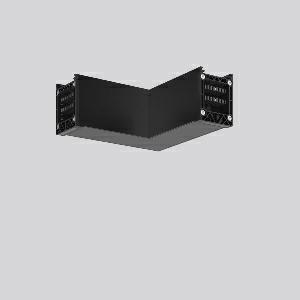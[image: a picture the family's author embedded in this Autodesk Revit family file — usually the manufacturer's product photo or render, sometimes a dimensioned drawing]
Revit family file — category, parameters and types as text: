
# Revit family: linedo_l-verbindung_982773_003_4_29e0
name_source: partatom
category: Lighting Fixtures
units: mm (PartAtom-declared; Revit-internal decimal feet)

## family parameters
Cut with Voids When Loaded = No
Host = Face
Light Source = No
Part Type = Normal
Room Calculation Point = No
Round Connector Dimension = Use Diameter
Shared = No

## types (1)
- LINEDO L-Verbindung
    Apparent Load = 0 VA
    Default Elevation = 1800 mm
    Description = Series: LINEDO
L-connector, 7-pole, connection socket / socket. Housing: extruded aluminium profile, powder-coated. Cover made of plastic, surface like housing. LINEDO plug system, plastic, black. Easy connection for rigid or flexible wires. 2 membrane cable entries (M25). Suitable for power supply in 7-pole version. Ready prewired. Colour-coded individual cables enable easy electromechanical separation.
Colour: jet black (RAL 9005)
Length: 185 mm
Width: 185 mm
Height: 76 mm
Weight: 640 g
    Height = 76 mm
    Lamp = 0 x
    Length = 185 mm
    Luminous efficacy = 0 lm/W
    Manufacturer = RZB
    ModVariant = No
    Model = 982773.003.4
    Mounting Place = Ceiling
    Mounting Type = Surface mounted
    Number of Poles = 1
    OnlyDefault = Yes
    Power Factor = 1
    Product Name = LINEDO L-Verbindung
    Product group = Surface mounted continuous line luminaire system
    ProductGroupID = 310
    Protection Class = Protection class I
    Protection Degree = Degree of protection
    RLX_Detail_Level = 1
    RLX_Emergency_Light_Flux = 0 lm
    RLX_Emergency_Type = 0
    RLX_Emergency_Type_DB = No
    RlxData = <blob elided: 18985 chars, md5=64a5a9c9>
    Standby Power = 0 W
    System Light Flux = 0 lm
    System Power = 0 W
    Type Comments = Product without accessories
    Type Image = 982773.003.1.jpg
    URL = http://relux.com
    VarID = ---
    Voltage = 0 V
    Weight = 0.00 kg
    Width = 185 mm

## geometry (parser evidence)
native form markers: Blend x4, Sweep x10
no freeform markers — native parametric forms only
